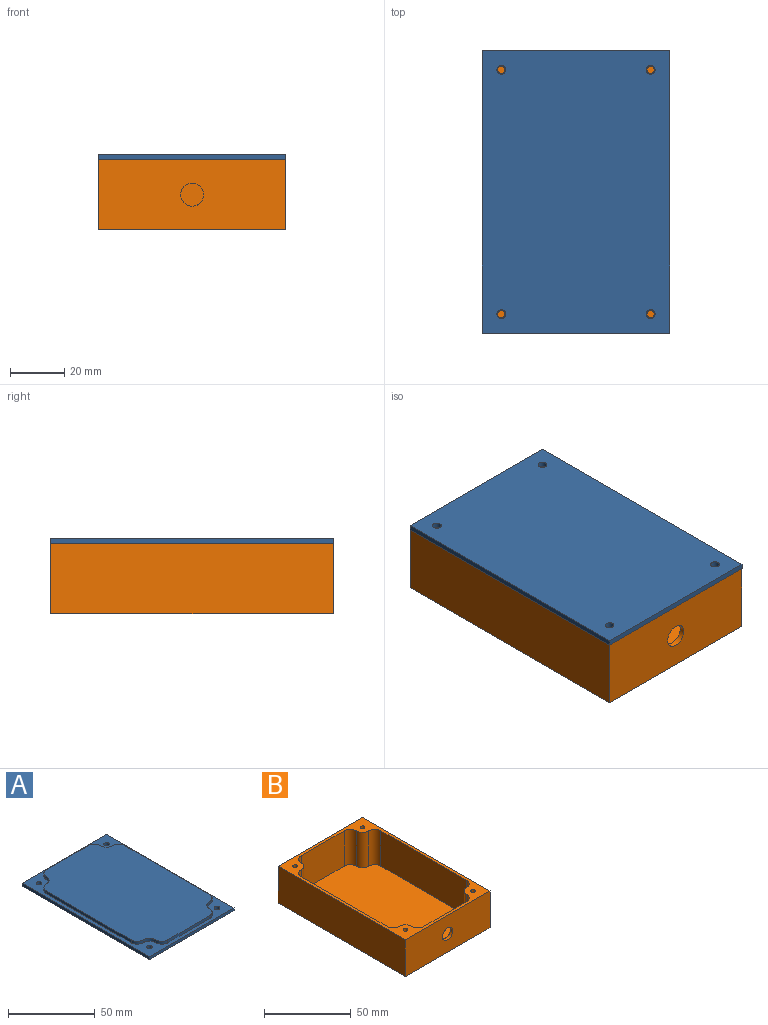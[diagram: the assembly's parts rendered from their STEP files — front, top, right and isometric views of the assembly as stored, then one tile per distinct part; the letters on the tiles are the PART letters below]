
ASSEMBLY  parts=2 mates=1
PART A: 27 faces, bbox 69x104x4 mm
  f0: plane 34x2mm, normal (0,-1,0), area 68mm2, adj f4,f9,f17,f24
  f1: plane 69x2mm, normal (1,0,0), area 138mm2, adj f4,f9,f15,f20
  f2: plane 34x2mm, normal (0,1,0), area 68mm2, adj f4,f9,f18,f23
  f3: plane 69x2mm, normal (-1,0,0), area 138mm2, adj f4,f9,f21,f26
  f4: plane 99x64mm, normal (0,0,1), area 5914.5mm2, adj f0,f1,f2,f3,f15,f16,f17,f18
  f5: plane 104x2mm, normal (-1,0,0), area 208mm2, adj f6,f8,f9,f10
  f6: plane 69x2mm, normal (0,-1,0), area 138mm2, adj f5,f7,f9,f10
  f7: plane 104x2mm, normal (1,0,0), area 208mm2, adj f6,f8,f9,f10
  f8: plane 69x2mm, normal (0,1,0), area 138mm2, adj f5,f7,f9,f10
  f9: plane 104x69mm, normal (0,0,1), area 1228.3mm2, adj f0,f1,f2,f3,f5,f6,f7,f8
  f10: plane 104x69mm, normal (0,0,-1), area 7142.8mm2, adj f5,f6,f7,f8,f11,f12,f13,f14
  f11: cylinder r=1.62mm len=3.25mm, axis (0,0,-1), area 20.4mm2, adj f9,f10
  f12: cylinder r=1.62mm len=3.25mm, axis (0,0,-1), area 20.4mm2, adj f9,f10
  f13: cylinder r=1.62mm len=3.25mm, axis (0,0,-1), area 20.4mm2, adj f9,f10
  f14: cylinder r=1.62mm len=3.25mm, axis (0,0,-1), area 20.4mm2, adj f9,f10
  f15: cylinder r=5mm len=5mm, axis (0,0,1), area 15.7mm2, adj f1,f4,f9,f16
  f16: cylinder r=5mm len=5mm, axis (0,0,1), area 15.7mm2, adj f4,f9,f15,f17
  f17: cylinder r=5mm len=5mm, axis (0,0,1), area 15.7mm2, adj f0,f4,f9,f16
  f18: cylinder r=5mm len=5mm, axis (0,0,-1), area 15.7mm2, adj f2,f4,f9,f19
  f19: cylinder r=5mm len=5mm, axis (0,0,1), area 15.7mm2, adj f4,f9,f18,f20
  f20: cylinder r=5mm len=5mm, axis (0,0,-1), area 15.7mm2, adj f1,f4,f9,f19
  f21: cylinder r=5mm len=5mm, axis (0,0,-1), area 15.7mm2, adj f3,f4,f9,f22
  f22: cylinder r=5mm len=5mm, axis (0,0,1), area 15.7mm2, adj f4,f9,f21,f23
  f23: cylinder r=5mm len=5mm, axis (0,0,-1), area 15.7mm2, adj f2,f4,f9,f22
  f24: cylinder r=5mm len=5mm, axis (0,0,1), area 15.7mm2, adj f0,f4,f9,f25
  f25: cylinder r=5mm len=5mm, axis (0,0,1), area 15.7mm2, adj f4,f9,f24,f26
  f26: cylinder r=5mm len=5mm, axis (0,0,1), area 15.7mm2, adj f3,f4,f9,f25
PART B: 39 faces, bbox 69x104x26 mm
  f0: plane 70x25mm, normal (-1,0,0), area 1750mm2, adj f1,f10,f30,f38
  f1: plane 100x65mm, normal (0,0,1), area 5938.5mm2, adj f0,f2,f3,f4,f12,f13,f14,f15
  f2: plane 35x26mm, normal (0,1,0), area 828.3mm2, adj f1,f5,f10,f11,f16,f17,f27,f32
  f3: plane 70x25mm, normal (1,0,0), area 1750mm2, adj f1,f10,f28,f33
  f4: plane 35x25mm, normal (0,-1,0), area 875mm2, adj f1,f10,f35,f36
  f5: plane 104x69mm, normal (0,0,-1), area 7036mm2, adj f2,f6,f7,f8,f9,f12,f13,f14
  f6: plane 104x26mm, normal (-1,0,0), area 2704mm2, adj f5,f7,f9,f10
  f7: plane 69x26mm, normal (0,-1,0), area 1737.3mm2, adj f5,f6,f8,f10,f11
  f8: plane 104x26mm, normal (1,0,0), area 2704mm2, adj f5,f7,f9,f10
  f9: plane 69x26mm, normal (0,1,0), area 1794mm2, adj f5,f6,f8,f10
  f10: plane 104x69mm, normal (0,0,1), area 1073.7mm2, adj f0,f2,f3,f4,f6,f7,f8,f9
  f11: cylinder r=4.25mm len=8.5mm, axis (0,-1,0), area 53.4mm2, adj f2,f7
  f12: plane 10x1mm, normal (0,1,0), area 10mm2, adj f1,f5,f13,f15
  f13: plane 7x1mm, normal (-1,0,0), area 7mm2, adj f1,f5,f12,f14
  f14: plane 10x1mm, normal (0,-1,0), area 10mm2, adj f1,f5,f13,f15
  f15: plane 7x1mm, normal (1,0,0), area 7mm2, adj f1,f5,f12,f14
  f16: plane 7x1mm, normal (1,0,0), area 7mm2, adj f1,f2,f5,f18
  f17: plane 7x1mm, normal (-1,0,0), area 7mm2, adj f1,f2,f5,f18
  f18: plane 10x1mm, normal (0,-1,0), area 10mm2, adj f1,f5,f16,f17
  f19: cylinder r=1.38mm len=25mm, axis (0,0,-1), area 216mm2, adj f10,f20
  f20: plane 2.75x2.75mm, normal (0,0,1), area 5.9mm2, adj f19
  f21: cylinder r=1.38mm len=25mm, axis (0,0,-1), area 216mm2, adj f10,f22
  f22: plane 2.75x2.75mm, normal (0,0,1), area 5.9mm2, adj f21
  f23: cylinder r=1.38mm len=25mm, axis (0,0,-1), area 216mm2, adj f10,f24
  f24: plane 2.75x2.75mm, normal (0,0,1), area 5.9mm2, adj f23
  f25: cylinder r=1.38mm len=25mm, axis (0,0,-1), area 216mm2, adj f10,f26
  f26: plane 2.75x2.75mm, normal (0,0,1), area 5.9mm2, adj f25
  f27: cylinder r=5mm len=25mm, axis (0,0,1), area 196.3mm2, adj f1,f2,f10,f29
  f28: cylinder r=5mm len=25mm, axis (0,0,-1), area 196.3mm2, adj f1,f3,f10,f29
  f29: cylinder r=5mm len=25mm, axis (0,0,1), area 196.3mm2, adj f1,f10,f27,f28
  f30: cylinder r=5mm len=25mm, axis (0,0,1), area 196.3mm2, adj f0,f1,f10,f31
  f31: cylinder r=5mm len=25mm, axis (0,0,-1), area 196.3mm2, adj f1,f10,f30,f32
  f32: cylinder r=5mm len=25mm, axis (0,0,1), area 196.3mm2, adj f1,f2,f10,f31
  f33: cylinder r=5mm len=25mm, axis (0,0,1), area 196.3mm2, adj f1,f3,f10,f34
  f34: cylinder r=5mm len=25mm, axis (0,0,1), area 196.3mm2, adj f1,f10,f33,f35
  f35: cylinder r=5mm len=25mm, axis (0,0,-1), area 196.3mm2, adj f1,f4,f10,f34
  f36: cylinder r=5mm len=25mm, axis (0,0,1), area 196.3mm2, adj f1,f4,f10,f37
  f37: cylinder r=5mm len=25mm, axis (0,0,-1), area 196.3mm2, adj f1,f10,f36,f38
  f38: cylinder r=5mm len=25mm, axis (0,0,1), area 196.3mm2, adj f0,f1,f10,f37
PLACE A rot(axis=(1,0,0),180deg) t=(86.45,39.95,-30.6)mm
PLACE B rot(axis=(0,-1,-0.02),0deg) t=(54.95,88.95,-58.6)mm
MATE slider B.f19 <-> A.f11  axis (0,0,1) through (114.95,83.95,-57.6)mm
